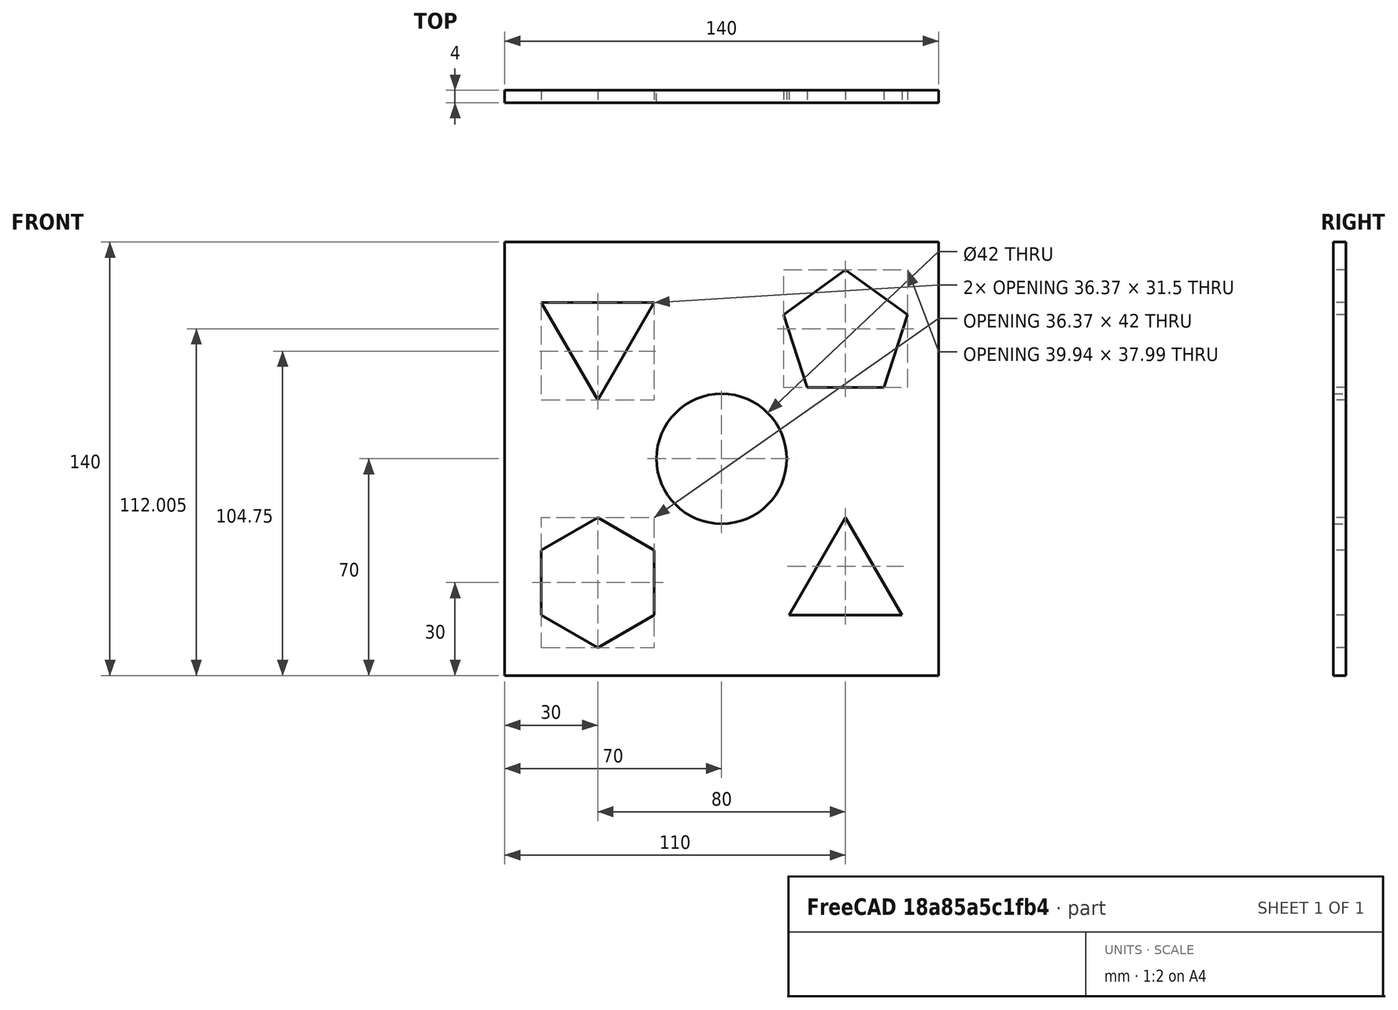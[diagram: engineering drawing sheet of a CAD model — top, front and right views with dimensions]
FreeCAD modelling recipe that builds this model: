
FCSTD DOCUMENT  (FreeCAD 2023.521R14555 (Git shallow))
Label: Main_board
License: All rights reserved
objects: PartDesign::CoordinateSystem×5, Sketcher::SketchObject×2, PartDesign::Pad×1, Spreadsheet::Sheet×1, PartDesign::Body×1, App::Part×1
note: 13 computed .brp shape members not serialized (recipe doc carries the construction recipe); baked Part::Feature solids carry a one-line shape summary decoded from their .brp

FEATURE [Sketcher::SketchObject] Sketch
  ArcFitTolerance = 1e-06
  AttachmentSupport = -> [XZ_Plane]
  ExternalBSplineMaxDegree = 5
  ExternalBSplineTolerance = 0.0001
  FullyConstrained = true
  InternalTolerance = 1e-06
  InvalidShape = false
  MakeInternals = false
  MapMode = 5
  Placement = pos=(0,0,0) rot=(1,0,0;1.5708rad)
  Support = -> [XZ_Plane]
  TreeRank = 11
  ValidateShape = false
  expr: Constraints[48] = <<dims>>.HS
  sketch-geometry (31):
    g0: LineSegment StartX=-40 StartY=19 StartZ=0 EndX=-21.8135 EndY=50.5 EndZ=0
    g1: LineSegment StartX=-21.8135 StartY=50.5 StartZ=0 EndX=-58.1865 EndY=50.5 EndZ=0
    g2: LineSegment StartX=-58.1865 StartY=50.5 StartZ=0 EndX=-40 EndY=19 EndZ=0
    g3: Circle [constr] CenterX=-40 CenterY=40 CenterZ=0 NormalX=0 NormalY=0 NormalZ=1 AngleXU=0 Radius=21
    g4: LineSegment StartX=40 StartY=-19 StartZ=0 EndX=21.8135 EndY=-50.5 EndZ=0
    g5: LineSegment StartX=21.8135 StartY=-50.5 StartZ=0 EndX=58.1865 EndY=-50.5 EndZ=0
    g6: LineSegment StartX=58.1865 StartY=-50.5 StartZ=0 EndX=40 EndY=-19 EndZ=0
    g7: Circle [constr] CenterX=40 CenterY=-40 CenterZ=0 NormalX=0 NormalY=0 NormalZ=1 AngleXU=0 Radius=21
    g8: LineSegment StartX=27.6565 StartY=23.0106 StartZ=0 EndX=52.3435 EndY=23.0106 EndZ=0
    g9: LineSegment StartX=52.3435 StartY=23.0106 StartZ=0 EndX=59.9722 EndY=46.4894 EndZ=0
    g10: LineSegment StartX=59.9722 StartY=46.4894 StartZ=0 EndX=40 EndY=61 EndZ=0
    g11: LineSegment StartX=40 StartY=61 StartZ=0 EndX=20.0278 EndY=46.4894 EndZ=0
    g12: LineSegment StartX=20.0278 StartY=46.4894 StartZ=0 EndX=27.6565 EndY=23.0106 EndZ=0
    g13: Circle [constr] CenterX=40 CenterY=40 CenterZ=0 NormalX=0 NormalY=0 NormalZ=1 AngleXU=0 Radius=21
    g14: LineSegment StartX=-21.8135 StartY=-29.5 StartZ=0 EndX=-40 EndY=-19 EndZ=0
    g15: LineSegment StartX=-40 StartY=-19 StartZ=0 EndX=-58.1865 EndY=-29.5 EndZ=0
    g16: LineSegment StartX=-58.1865 StartY=-29.5 StartZ=0 EndX=-58.1865 EndY=-50.5 EndZ=0
    g17: LineSegment StartX=-58.1865 StartY=-50.5 StartZ=0 EndX=-40 EndY=-61 EndZ=0
    g18: LineSegment StartX=-40 StartY=-61 StartZ=0 EndX=-21.8135 EndY=-50.5 EndZ=0
    g19: LineSegment StartX=-21.8135 StartY=-50.5 StartZ=0 EndX=-21.8135 EndY=-29.5 EndZ=0
    g20: Circle [constr] CenterX=-40 CenterY=-40 CenterZ=0 NormalX=0 NormalY=0 NormalZ=1 AngleXU=0 Radius=21
    g21: Circle CenterX=0 CenterY=0 CenterZ=0 NormalX=0 NormalY=0 NormalZ=1 AngleXU=0 Radius=21
    g22: LineSegment [constr] StartX=-40 StartY=40 StartZ=0 EndX=40 EndY=40 EndZ=0
    g23: LineSegment [constr] StartX=40 StartY=40 StartZ=0 EndX=40 EndY=-40 EndZ=0
    g24: LineSegment [constr] StartX=40 StartY=-40 StartZ=0 EndX=-40 EndY=-40 EndZ=0
    g25: LineSegment [constr] StartX=-40 StartY=-40 StartZ=0 EndX=-40 EndY=40 EndZ=0
    g26: LineSegment StartX=-70 StartY=-70 StartZ=0 EndX=-70 EndY=70 EndZ=0
    g27: LineSegment StartX=-70 StartY=70 StartZ=0 EndX=70 EndY=70 EndZ=0
    g28: LineSegment StartX=70 StartY=70 StartZ=0 EndX=70 EndY=-70 EndZ=0
    g29: LineSegment StartX=70 StartY=-70 StartZ=0 EndX=-70 EndY=-70 EndZ=0
    g30: GeomPoint [constr] X=0 Y=0 Z=0
  constraints (77):
    c: Coincident(g0,g1)
    c: Coincident(g1,g2)
    c: Coincident(g2,g0)
    c: Equal(g0,g1)
    c: Equal(g0,g2)
    c: PointOnObject(g0,g3)
    c: PointOnObject(g1,g3)
    c: PointOnObject(g2,g3)
    c: Coincident(g4,g5)
    c: Coincident(g5,g6)
    c: Coincident(g6,g4)
    c: Equal(g4,g5)
    c: Equal(g4,g6)
    c: PointOnObject(g4,g7)
    c: PointOnObject(g5,g7)
    c: PointOnObject(g6,g7)
    c: Coincident(g8,g9)
    c: Coincident(g9,g10)
    c: Coincident(g10,g11)
    c: Coincident(g11,g12)
    c: Coincident(g12,g8)
    c: Equal(g8, g9-g12) x4
    c: PointOnObject(g8,g13)
    c: PointOnObject(g9,g13)
    c: PointOnObject(g10,g13)
    c: PointOnObject(g11,g13)
    c: PointOnObject(g12,g13)
    c: Coincident(g14,g15)
    c: Coincident(g15,g16)
    c: Coincident(g16,g17)
    c: Coincident(g17,g18)
    c: Coincident(g18,g19)
    c: Coincident(g19,g14)
    c: Equal(g14, g15-g19) x5
    c: PointOnObject(g14,g20)
    c: PointOnObject(g15,g20)
    c: PointOnObject(g16,g20)
    c: PointOnObject(g17,g20)
    c: PointOnObject(g18,g20)
    c: PointOnObject(g19,g20)
    c: Coincident(g21,g-1)
    c: Diameter(g13) = 42
    c: Horizontal(g8)
    c: Equal(g13,g7)
    c: Equal(g7,g20)
    c: Equal(g20,g3)
    c: Vertical(g19)
    c: Horizontal(g5)
    c: Horizontal(g1)
    c: Coincident(g22,g23)
    c: Coincident(g23,g24)
    c: Coincident(g24,g25)
    c: Coincident(g25,g22)
    c: Horizontal(g22)
    c: Horizontal(g24)
    c: Vertical(g23)
    c: Vertical(g25)
    c: Coincident(g22,g3)
    c: Coincident(g23,g7)
    c: Coincident(g22,g13)
    c: Coincident(g24,g20)
    c: Symmetric(g24,g22,g21)
    c: Equal(g23,g24)
    c: DistanceY(g23,g23) = 80
    c: Coincident(g26,g27)
    c: Coincident(g27,g28)
    c: Coincident(g28,g29)
    c: Coincident(g29,g26)
    c: Horizontal(g27)
    c: Horizontal(g29)
    c: Vertical(g26)
    c: Vertical(g28)
    c: Symmetric(g27,g26,g30)
    c: Coincident(g30,g21)
    c: Equal(g28,g29)
    c: DistanceY(g28,g28) = 140
    c: Equal(g21,g13)
FEATURE [PartDesign::Pad] Pad
  AddSubType = 0
  AlongSketchNormal = false
  AutoTaperInnerAngle = true
  CheckUpToFaceLimits = true
  ClaimChildren = false
  Direction = (0,-1,-2e-16)
  Fit = 0
  FitJoin = 0
  InnerFit = 0
  InnerFitJoin = 0
  InvalidShape = false
  Length = 4
  Length2 = 10
  Linearize = true
  NewSolid = false
  Profile = -> Sketch
  ReferenceAxis = -> Sketch [N_Axis]
  Suppress = false
  TaperInnerAngle = 0
  TaperInnerAngleRev = 0
  TreeRank = 12
  Type = 0
  ValidateShape = true
  _ProfileBasedVersion = 1
FEATURE [PartDesign::CoordinateSystem] Local_CS  label="Triangle0"
  AttacherType = Attacher::AttachEngine3D
  AttachmentSupport = -> [Pad]
  InvalidShape = false
  MapMode = 13
  Placement = pos=(-40,-4,40) rot=(1,0,0;1.5708rad)
  Support = -> [Pad]
  TreeRank = 16
  ValidateShape = false
FEATURE [PartDesign::CoordinateSystem] Local_CS002  label="Triangle1"
  AttacherType = Attacher::AttachEngine3D
  AttachmentOffset = pos=(0,0,0) rot=(0,0,1;3.14159rad)
  AttachmentSupport = -> [Pad]
  InvalidShape = false
  MapMode = 13
  Placement = pos=(40,-4,-40) rot=(0,-0.707107,0.707107;3.14159rad)
  Support = -> [Pad]
  TreeRank = 21
  ValidateShape = false
FEATURE [PartDesign::CoordinateSystem] Local_CS003  label="Circle"
  AttacherType = Attacher::AttachEngine3D
  AttachmentSupport = -> [Pad]
  InvalidShape = false
  MapMode = 11
  Placement = pos=(0,-4,-9e-16) rot=(0.57735,-0.57735,0.57735;2.0944rad)
  Support = -> [Pad]
  TreeRank = 22
  ValidateShape = false
FEATURE [Spreadsheet::Sheet] Spreadsheet  label="dims"
  PythonMode = false
  ShowCells = 0
  TreeRank = 25
  cells = A1=Part SIze; B1(PS)==40mm; A2=Gap; B2==2mm; A3=Hole Size; B3(HS)==B1 + B2
FEATURE [Sketcher::SketchObject] Sketch001
  ArcFitTolerance = 1e-06
  AttachmentSupport = -> [Pad]
  ExternalBSplineMaxDegree = 5
  ExternalBSplineTolerance = 0.0001
  ExternalGeometry = -> [Pad]
  FullyConstrained = true
  InternalTolerance = 1e-06
  InvalidShape = false
  MakeInternals = false
  MapMode = 5
  Placement = pos=(0,-4,-9e-16) rot=(1,0,0;1.5708rad)
  Support = -> [Pad]
  TreeRank = 26
  ValidateShape = false
  sketch-geometry (2):
    g0: Circle CenterX=40 CenterY=40 CenterZ=0 NormalX=0 NormalY=0 NormalZ=1 AngleXU=0 Radius=21
    g1: Circle CenterX=-40 CenterY=-40 CenterZ=0 NormalX=0 NormalY=0 NormalZ=1 AngleXU=0 Radius=21
  constraints (6):
    c: PointOnObject(g-4,g0)
    c: PointOnObject(g-3,g0)
    c: PointOnObject(g-3,g0)
    c: PointOnObject(g-5,g1)
    c: PointOnObject(g-6,g1)
    c: PointOnObject(g-6,g1)
FEATURE [PartDesign::Body] Body
  AutoGroupSolids = false
  ClaimAllChildren = false
  ExportMode = 0
  Group = -> [Sketch,Pad,Sketch001]
  InvalidShape = false
  Origin = -> Origin
  Tip = -> Pad
  TreeRank = 10
  ValidateShape = false
  _ExportChildren = -> [Pad,Sketch001]
  _GroupVersion = 1
FEATURE [PartDesign::CoordinateSystem] Local_CS004  label="Penta"
  AttacherType = Attacher::AttachEngine3D
  AttachmentSupport = -> [Sketch001]
  InvalidShape = false
  MapMode = 11
  Placement = pos=(40,-4,40) rot=(-0.57735,0.57735,-0.57735;4.18879rad)
  Support = -> [Sketch001]
  TreeRank = 23
  ValidateShape = false
FEATURE [PartDesign::CoordinateSystem] Local_CS005  label="Hex"
  AttacherType = Attacher::AttachEngine3D
  AttachmentSupport = -> [Sketch001]
  InvalidShape = false
  MapMode = 11
  Placement = pos=(-40,-4,-40) rot=(-0.57735,0.57735,-0.57735;4.18879rad)
  Support = -> [Sketch001]
  TreeRank = 24
  ValidateShape = false
FEATURE [App::Part] Part
  ClaimAllChildren = false
  ExportMode = 1
  Group = -> [Body,Local_CS,Local_CS002,Local_CS003,Local_CS004,Local_CS005]
  Origin = -> Origin001
  TreeRank = 15
  _ExportChildren = -> [Body,Local_CS,Local_CS002,Local_CS003,Local_CS004,Local_CS005]
  _GroupVersion = 1
